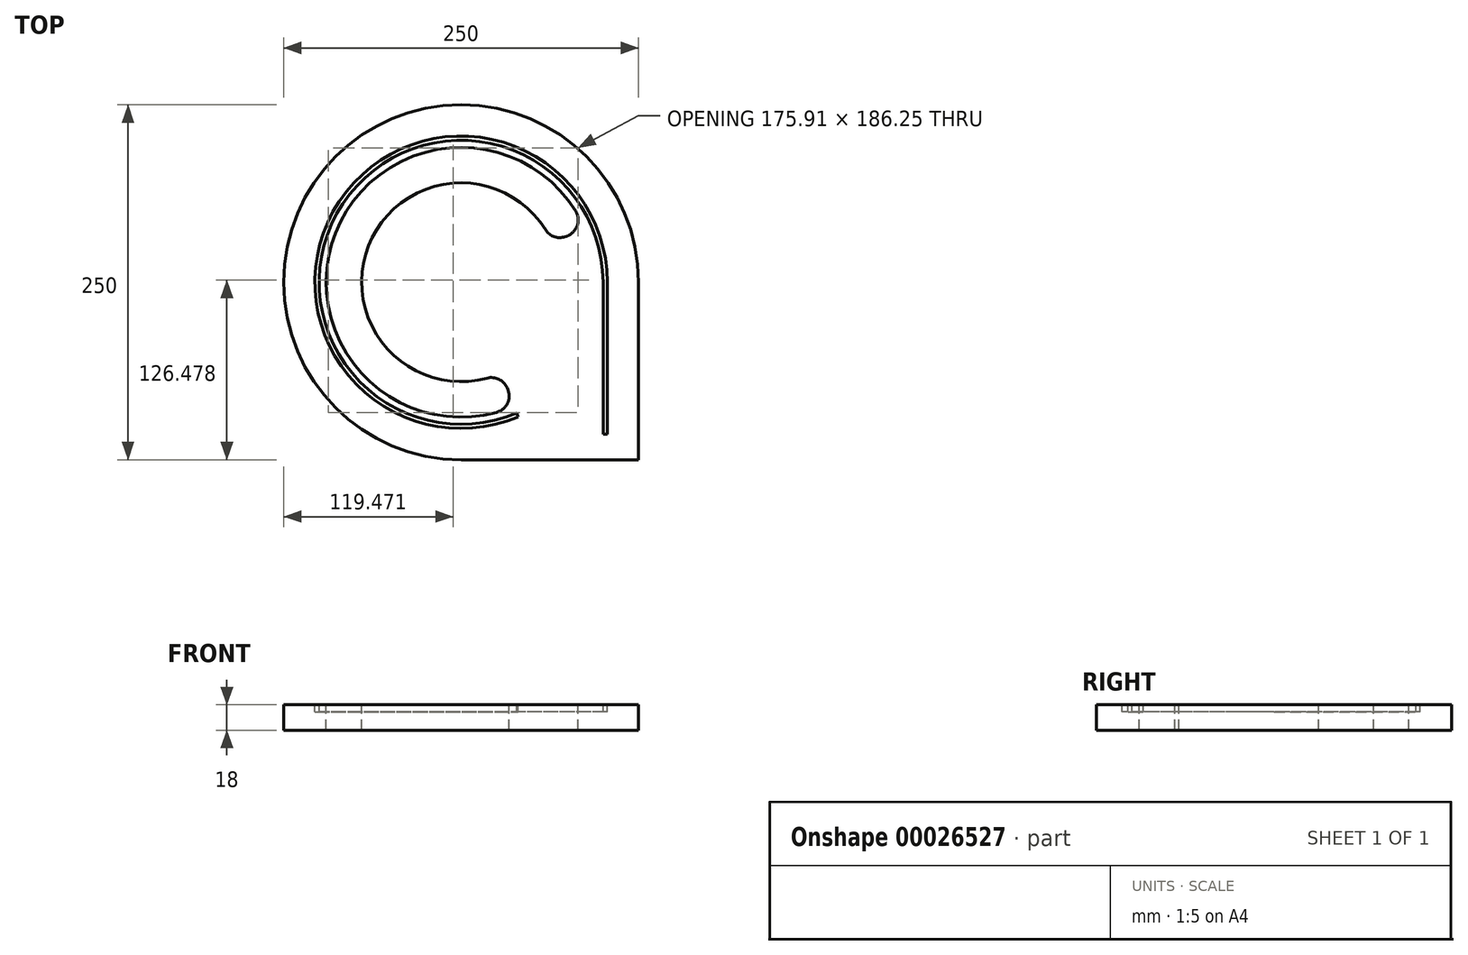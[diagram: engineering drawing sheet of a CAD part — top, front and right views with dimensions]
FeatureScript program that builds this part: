
annotation { "Feature Type Name" : "Feature", "Feature Type Description" : "" }
export const myFeature = defineFeature(function(context is Context, id is Id, definition is map)
    precondition{}
    {
        {
            var Q0;
            Q0=qCreatedBy(makeId("Top.planeOp"),FACE);
            var sketch = newSketch(context, id + "F0", { "sketchPlane" : qUnion([Q0])});
            skArc(sketch, "E0", {"start": v(80.66, 50.19) * mm, "mid": v(-88.44, 34.7) * mm, "end": v(25.01, -91.65) * mm});
            skArc(sketch, "E1", {"start": v(100, 0) * mm, "mid": v(-83.42, 55.15) * mm, "end": v(39.16, -92.01) * mm});
            skLineSegment(sketch, "E2", {"start": v(103, 0) * mm, "end": v(103, -125) * mm});
            skLineSegment(sketch, "E3", {"start": v(100, 0) * mm, "end": v(100, -107) * mm});
            skLineSegment(sketch, "E4", {"start": v(22, -100.11) * mm, "end": v(22, -125) * mm});
            skLineSegment(sketch, "E5", {"start": v(103, -107) * mm, "end": v(22, -107) * mm});
            skLineSegment(sketch, "E6", {"start": v(125, 0) * mm, "end": v(124.89, -125) * mm});
            skLineSegment(sketch, "E7", {"start": v(32.85, -75.27) * mm, "end": v(32.45, -74.35) * mm});
            skLineSegment(sketch, "E8", {"start": v(74.35, 32.45) * mm, "end": v(75.27, 32.85) * mm});
            skArc(sketch, "E9", {"start": v(59.37, 37.09) * mm, "mid": v(-65.16, 25.57) * mm, "end": v(18.3, -67.56) * mm});
            skPoint(sketch, "E10.visualSharp", {"position": v(87.07, 38) * mm});
            skArc(sketch, "E10.filletArc", {"start": v(75.27, 32.85) * mm, "mid": v(81.93, 40.29) * mm, "end": v(80.66, 50.19) * mm});
            skPoint(sketch, "E11.visualSharp", {"position": v(64.16, 28) * mm});
            skArc(sketch, "E11.filletArc", {"start": v(59.37, 37.09) * mm, "mid": v(66, 31.98) * mm, "end": v(74.35, 32.45) * mm});
            skPoint(sketch, "E12.visualSharp", {"position": v(28, -64.16) * mm});
            skArc(sketch, "E12.filletArc", {"start": v(32.45, -74.35) * mm, "mid": v(26.64, -68.33) * mm, "end": v(18.3, -67.56) * mm});
            skPoint(sketch, "E13.visualSharp", {"position": v(38, -87.07) * mm});
            skArc(sketch, "E13.filletArc", {"start": v(25.01, -91.65) * mm, "mid": v(32.68, -85.25) * mm, "end": v(32.85, -75.27) * mm});
            skLineSegment(sketch, "E14", {"start": v(40, -94.92) * mm, "end": v(39.16, -92.01) * mm});
            skArc(sketch, "E15", {"start": v(125, -0.22) * mm, "mid": v(-88.3, 88.47) * mm, "end": v(0, -125) * mm});
            skLineSegment(sketch, "E16", {"start": v(0, -125) * mm, "end": v(22, -125) * mm});
            skLineSegment(sketch, "E17", {"start": v(22, -125) * mm, "end": v(124.89, -125) * mm});
            skLineSegment(sketch, "E18", {"start": v(100, -89) * mm, "end": v(51.85, -89) * mm});
            skArc(sketch, "E19", {"start": v(103, 0) * mm, "mid": v(-102.25, 12.43) * mm, "end": v(100, -24.68) * mm});
            skSolve(sketch);
        }
        {
            var Q0;
            {var subQ5=sQuery(id+"F0.wireOp",EDGE,"E16");Q0=makeQuery(id+"F0.imprint","IMPRINT",FACE,{"disambiguationData":[TD([[makeQuery(id+"F0.imprint","IMPRINT",EDGE,{"derivedFrom":subQ5}),1.0]])]});}
            var Q1;
            {var subQ1=sQuery(id+"F0.wireOp",EDGE,"E18");Q1=makeQuery(id+"F0.imprint","IMPRINT",FACE,{"disambiguationData":[TD([[makeQuery(id+"F0.imprint","IMPRINT",EDGE,{"derivedFrom":subQ1}),1.0]])]});}
            var Q2;
            Q2=makeQuery(id+"F0.imprint","IMPRINT",FACE,{"disambiguationData":[TD([[makeQuery(id+"F0.imprint","IMPRINT",EDGE,{"derivedFrom":sQuery(id+"F0.wireOp",EDGE,"E0")}),-1.0]])]});
            var Q3;
            {var subQ3=sQuery(id+"F0.wireOp",EDGE,"E18");Q3=makeQuery(id+"F0.imprint","IMPRINT",FACE,{"disambiguationData":[TD([[makeQuery(id+"F0.imprint","IMPRINT",EDGE,{"derivedFrom":subQ3}),-1.0]])]});}
            var Q4;
            {var subQ0=sQuery(id+"F0.wireOp",EDGE,"E19");var subQ3=sQuery(id+"F0.wireOp",EDGE,"E2");var subQ4=makeQuery(id+"F0.imprint","INTERSECT",VERTEX,{"derivedFrom":[subQ3,subQ0]});Q4=makeQuery(id+"F0.imprint","IMPRINT",FACE,{"disambiguationData":[TD([[makeQuery(id+"F0.imprint","IMPRINT",EDGE,{"disambiguationData":[TD([[subQ4,-1.0]])],"derivedFrom":subQ3}),-1.0]])]});}
            var Q5;
            {var subQ6=sQuery(id+"F0.wireOp",EDGE,"E1");Q5=makeQuery(id+"F0.imprint","IMPRINT",FACE,{"disambiguationData":[TD([[makeQuery(id+"F0.imprint","IMPRINT",EDGE,{"derivedFrom":subQ6}),-1.0]])]});}
            var Q6;
            {var subQ0=sQuery(id+"F0.wireOp",EDGE,"E17");var subQ3=sQuery(id+"F0.wireOp",EDGE,"E2");var subQ4=makeQuery(id+"F0.imprint","INTERSECT",VERTEX,{"derivedFrom":[subQ3,subQ0]});Q6=makeQuery(id+"F0.imprint","IMPRINT",FACE,{"disambiguationData":[TD([[makeQuery(id+"F0.imprint","IMPRINT",EDGE,{"disambiguationData":[TD([[subQ4,1.0]])],"derivedFrom":subQ3}),-1.0]])]});}
            extrude(context, id + "F1", {"entities" : qUnion([Q0, Q1, Q2, Q3, Q4, Q5, Q6]), "oppositeDirection" : true, "depth" : 18 * mm});
        }
        {
            var Q0;
            {var subQ11=sQuery(id+"F0.wireOp",EDGE,"E1");Q0=makeQuery(id+"F0.imprint","IMPRINT",FACE,{"disambiguationData":[TD([[makeQuery(id+"F0.imprint","IMPRINT",EDGE,{"derivedFrom":subQ11}),-1.0]])]});}
            extrude(context, id + "F2", {"entities" : qUnion([Q0]), "operationType" : NewBodyOperationType.REMOVE, "oppositeDirection" : true, "depth" : 5 * mm});
        }
    });
